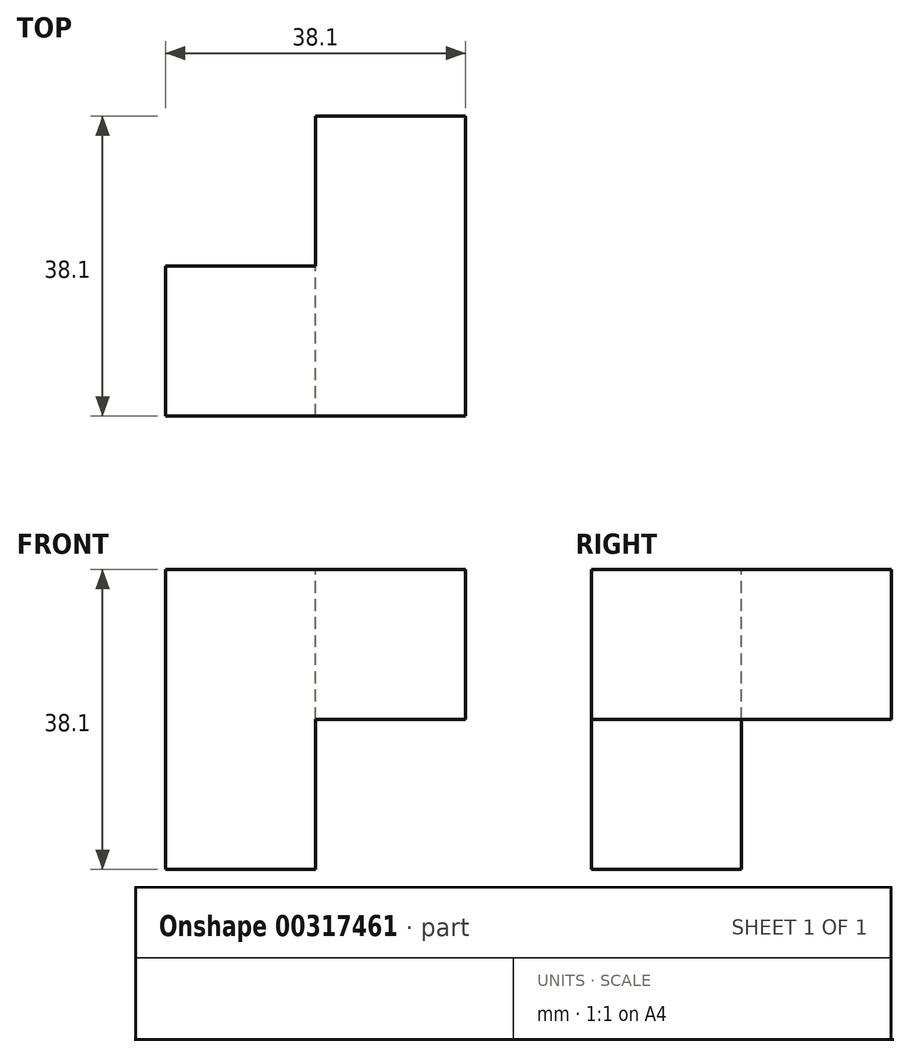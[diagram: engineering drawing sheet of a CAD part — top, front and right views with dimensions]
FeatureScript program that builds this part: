
annotation { "Feature Type Name" : "Feature", "Feature Type Description" : "" }
export const myFeature = defineFeature(function(context is Context, id is Id, definition is map)
    precondition{}
    {
        {
            var Q0;
            Q0=qCreatedBy(makeId("Front.planeOp"),FACE);
            var sketch = newSketch(context, id + "F0", { "sketchPlane" : qUnion([Q0])});
            skLineSegment(sketch, "E0.bottom", {"start": v(0, 0) * mm, "end": v(19.05, 0) * mm});
            skLineSegment(sketch, "E0.top", {"start": v(0, 38.1) * mm, "end": v(38.1, 38.1) * mm});
            skLineSegment(sketch, "E0.left", {"start": v(0, 0) * mm, "end": v(0, 38.1) * mm});
            skLineSegment(sketch, "E0.right", {"start": v(38.1, 19.05) * mm, "end": v(38.1, 38.1) * mm});
            skLineSegment(sketch, "E1.bottom", {"start": v(38.1, 19.05) * mm, "end": v(19.05, 19.05) * mm});
            skLineSegment(sketch, "E1.right", {"start": v(19.05, 19.05) * mm, "end": v(19.05, 0) * mm});
            skPoint(sketch, "E2.orphan", {"position": v(38.1, 0) * mm});
            skSolve(sketch);
        }
        {
            var Q0;
            Q0 = qSketchRegion(id + "F0", true);
            extrude(context, id + "F1", {"entities" : qUnion([Q0]), "depth" : 38.1 * mm});
        }
        {
            var Q0;
            Q0=makeQuery(id+"F1.opExtrude","SWEPT_FACE",FACE,{"disambiguationData":[OSD([sQuery(id+"F0.wireOp",EDGE,"E0.top")])]});
            var sketch = newSketch(context, id + "F2", { "sketchPlane" : qUnion([Q0])});
            skLineSegment(sketch, "E3.top", {"start": v(0, -19.05) * mm, "end": v(19.05, -19.05) * mm});
            skLineSegment(sketch, "E3.left", {"start": v(0, 0) * mm, "end": v(0, -19.05) * mm});
            skLineSegment(sketch, "E3.right", {"start": v(19.05, 0) * mm, "end": v(19.05, -19.05) * mm});
            skLineSegment(sketch, "E4", {"start": v(19.05, 0) * mm, "end": v(0, 0) * mm});
            skSolve(sketch);
        }
        {
            var Q0;
            Q0 = qSketchRegion(id + "F2", true);
            extrude(context, id + "F3", {"entities" : qUnion([Q0]), "operationType" : NewBodyOperationType.REMOVE, "endBound" : BoundingType.THROUGH_ALL, "oppositeDirection" : true, "depth" : 25.4 * mm});
        }
    });
